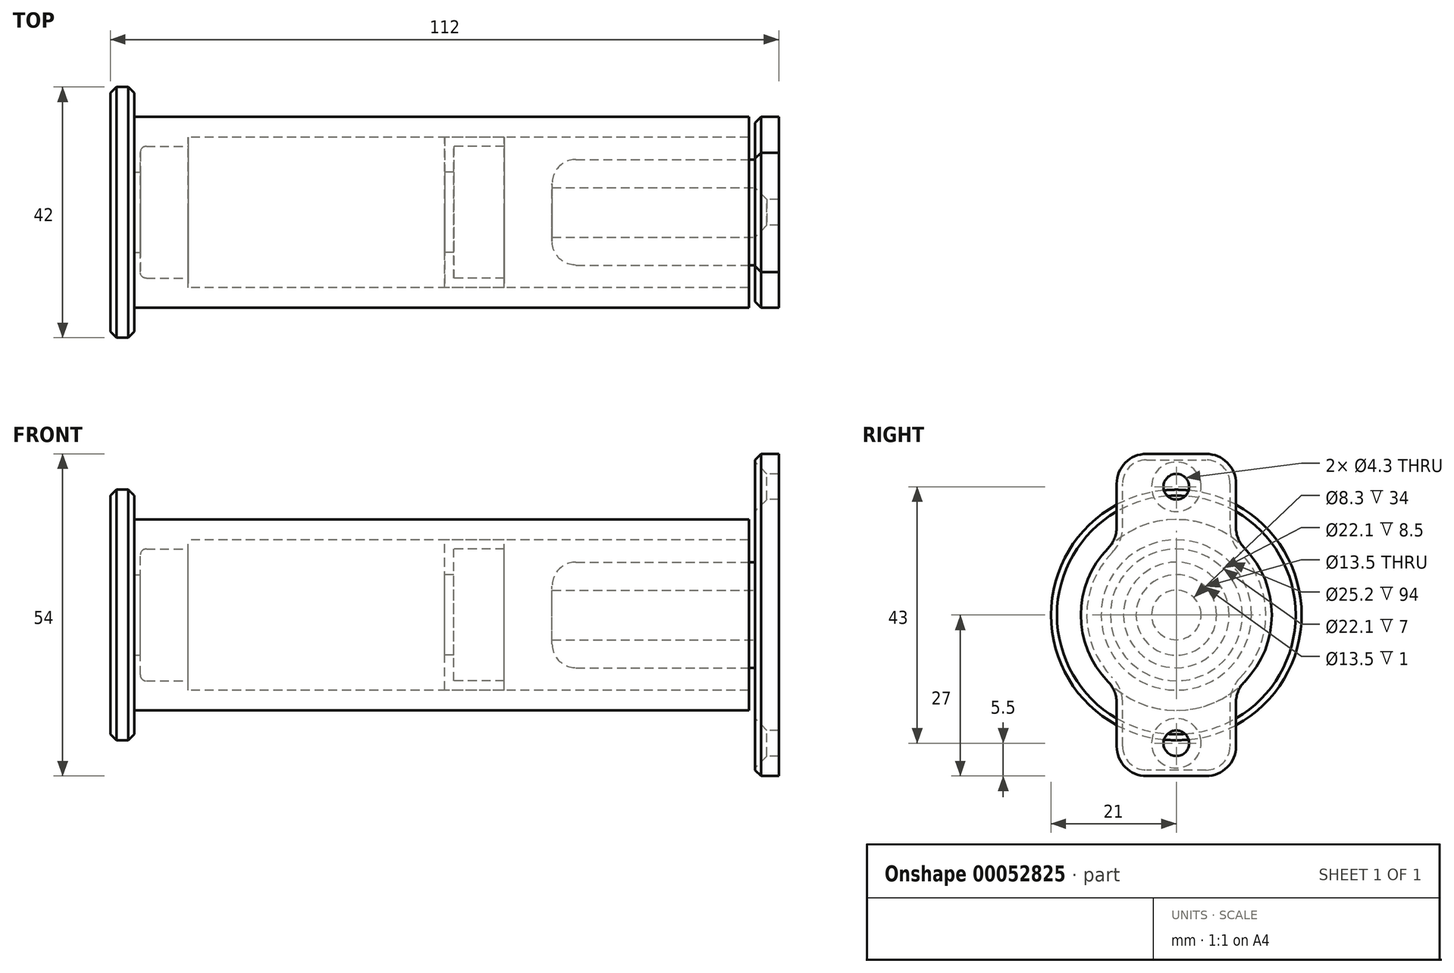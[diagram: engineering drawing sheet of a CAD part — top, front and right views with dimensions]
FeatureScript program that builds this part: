
annotation { "Feature Type Name" : "Feature", "Feature Type Description" : "" }
export const myFeature = defineFeature(function(context is Context, id is Id, definition is map)
    precondition{}
    {
        {
            var Q0;
            Q0=qCreatedBy(makeId("Right.planeOp"),FACE);
            var sketch = newSketch(context, id + "F0", { "sketchPlane" : qUnion([Q0])});
            skCircle(sketch, "E0", {"center": v(0, 0) * mm, "radius": 16 * mm});
            skCircle(sketch, "E1.0", {"center": v(0, 0) * mm, "radius": 12.6 * mm});
            skSolve(sketch);
        }
        {
            var Q0;
            Q0=makeQuery(id+"F0.imprint","IMPRINT",FACE,{"disambiguationData":[TD([[makeQuery(id+"F0.imprint","IMPRINT",EDGE,{"derivedFrom":sQuery(id+"F0.wireOp",EDGE,"E0")}),1.0]])]});
            extrude(context, id + "F1", {"entities" : qUnion([Q0]), "endBound" : BoundingType.SYMMETRIC, "depth" : 104 * mm});
        }
        {
            var Q0;
            Q0=makeQuery(id+"F1.opExtrude","CAP_FACE",FACE,{"disambiguationData":[OSD([sQuery(id+"F0.wireOp",EDGE,"E0"),sQuery(id+"F0.wireOp",EDGE,"E1.0")])],"isStart":true});
            var sketch = newSketch(context, id + "F2", { "sketchPlane" : qUnion([Q0])});
            skCircle(sketch, "E2.0", {"center": v(0, 0) * mm, "radius": 21 * mm});
            skSolve(sketch);
        }
        {
            var Q0;
            Q0=makeQuery(id+"F2.imprint","IMPRINT",FACE,{"disambiguationData":[TD([[makeQuery(id+"F2.imprint","IMPRINT",EDGE,{"derivedFrom":sQuery(id+"F2.wireOp",EDGE,"E2.0")}),1.0]])]});
            var Q1;
            Q1=makeQuery(id+"F2.imprint","IMPRINT",FACE,{"disambiguationData":[TD([[makeQuery(id+"F2.imprint","IMPRINT",EDGE,{"derivedFrom":makeQuery(id+"F1.opExtrude","CAP_EDGE",EDGE,{"disambiguationData":[OSD([sQuery(id+"F0.wireOp",EDGE,"E1.0")])],"isStart":true})}),-1.0]])]});
            var Q2;
            Q2=makeQuery(id+"F2.imprint","IMPRINT",FACE,{"disambiguationData":[TD([[makeQuery(id+"F2.imprint","IMPRINT",EDGE,{"derivedFrom":makeQuery(id+"F1.opExtrude","CAP_EDGE",EDGE,{"disambiguationData":[OSD([sQuery(id+"F0.wireOp",EDGE,"E0")])],"isStart":true})}),-1.0]])]});
            extrude(context, id + "F3", {"entities" : qUnion([Q0, Q1, Q2]), "depth" : 4 * mm});
        }
        {
            var Q0;
            Q0=makeQuery(id+"F2.imprint","IMPRINT",FACE,{"disambiguationData":[TD([[makeQuery(id+"F2.imprint","IMPRINT",EDGE,{"derivedFrom":makeQuery(id+"F1.opExtrude","CAP_EDGE",EDGE,{"disambiguationData":[OSD([sQuery(id+"F0.wireOp",EDGE,"E1.0")])],"isStart":true})}),-1.0]])]});
            extrude(context, id + "F4", {"entities" : qUnion([Q0]), "operationType" : NewBodyOperationType.ADD, "oppositeDirection" : true, "depth" : 9 * mm});
        }
        {
            var Q0;
            Q0=makeQuery(id+"F4.opExtrude","CAP_FACE",FACE,{"disambiguationData":[OSD([sQuery(id+"F0.wireOp",EDGE,"E1.0")])],"isStart":false});
            var sketch = newSketch(context, id + "F5", { "sketchPlane" : qUnion([Q0])});
            skCircle(sketch, "E3", {"center": v(0, 0) * mm, "radius": 11.05 * mm});
            skCircle(sketch, "E4", {"center": v(0, 0) * mm, "radius": 6.75 * mm});
            skSolve(sketch);
        }
        {
            var Q0;
            Q0=makeQuery(id+"F5.imprint","IMPRINT",FACE,{"disambiguationData":[TD([[makeQuery(id+"F5.imprint","IMPRINT",EDGE,{"derivedFrom":sQuery(id+"F5.wireOp",EDGE,"E3")}),1.0]])]});
            extrude(context, id + "F6", {"entities" : qUnion([Q0]), "operationType" : NewBodyOperationType.REMOVE, "oppositeDirection" : true, "depth" : 8 * mm});
        }
        {
            var Q0;
            Q0=makeQuery(id+"F6.boolean.opBoolean","SPLIT",FACE,{"disambiguationData":[TD([makeQuery(id+"F6.opExtrude","SWEPT_FACE",FACE,{"disambiguationData":[OSD([sQuery(id+"F5.wireOp",EDGE,"E4")])]})])],"derivedFrom":makeQuery(id+"F4.opExtrude","CAP_FACE",FACE,{"disambiguationData":[OSD([sQuery(id+"F0.wireOp",EDGE,"E1.0")])],"isStart":false})});
            extrude(context, id + "F7", {"entities" : qUnion([Q0]), "operationType" : NewBodyOperationType.REMOVE, "oppositeDirection" : true, "depth" : 9 * mm});
        }
        {
            var Q0;
            Q0=qCreatedBy(makeId("Right.planeOp"),FACE);
            var sketch = newSketch(context, id + "F8", { "sketchPlane" : qUnion([Q0])});
            skCircle(sketch, "E5.0", {"center": v(0, 0) * mm, "radius": 12.6 * mm});
            skCircle(sketch, "E5.1", {"center": v(0, 0) * mm, "radius": 11.05 * mm});
            skCircle(sketch, "E5.2", {"center": v(0, 0) * mm, "radius": 6.75 * mm});
            skSolve(sketch);
        }
        {
            var Q0;
            Q0=makeQuery(id+"F8.imprint","IMPRINT",FACE,{"disambiguationData":[TD([[makeQuery(id+"F8.imprint","IMPRINT",EDGE,{"derivedFrom":sQuery(id+"F8.wireOp",EDGE,"E5.0")}),1.0]])]});
            extrude(context, id + "F9", {"entities" : qUnion([Q0]), "depth" : 10 * mm});
        }
        {
            var Q0;
            Q0=makeQuery(id+"F8.imprint","IMPRINT",FACE,{"disambiguationData":[TD([[makeQuery(id+"F8.imprint","IMPRINT",EDGE,{"derivedFrom":sQuery(id+"F8.wireOp",EDGE,"E5.1")}),1.0]])]});
            extrude(context, id + "F10", {"entities" : qUnion([Q0]), "operationType" : NewBodyOperationType.ADD, "depth" : 1.5 * mm});
        }
        {
            var Q0;
            Q0=makeQuery(id+"F1.opExtrude","CAP_FACE",FACE,{"disambiguationData":[OSD([sQuery(id+"F0.wireOp",EDGE,"E0"),sQuery(id+"F0.wireOp",EDGE,"E1.0")])],"isStart":false});
            var sketch = newSketch(context, id + "F11", { "sketchPlane" : qUnion([Q0])});
            skCircle(sketch, "E6.0", {"center": v(0, 0) * mm, "radius": 16 * mm});
            skLineSegment(sketch, "E7.rect.bottom", {"start": v(5, -27) * mm, "end": v(-5, -27) * mm});
            skLineSegment(sketch, "E7.rect.top", {"start": v(5, 27) * mm, "end": v(-5, 27) * mm});
            skLineSegment(sketch, "E8", {"start": v(-16, 0) * mm, "end": v(16, 0) * mm, "construction": true});
            skLineSegment(sketch, "E9", {"start": v(0, -16) * mm, "end": v(0, -27) * mm, "construction": true});
            skCircle(sketch, "E10", {"center": v(0, -21.5) * mm, "radius": 2.15 * mm});
            skCircle(sketch, "E11.MirrorC", {"center": v(0, 21.5) * mm, "radius": 2.15 * mm});
            skLineSegment(sketch, "E12", {"start": v(10, -12.49) * mm, "end": v(10, -22) * mm});
            skLineSegment(sketch, "E13", {"start": v(-10, -22) * mm, "end": v(-10, -12.49) * mm});
            skLineSegment(sketch, "E14.MirrorCS", {"start": v(10, 12.49) * mm, "end": v(10, 22) * mm});
            skLineSegment(sketch, "E15.MirrorCS", {"start": v(-10, 22) * mm, "end": v(-10, 12.49) * mm});
            skPoint(sketch, "E16.visualSharp", {"position": v(10, 27) * mm});
            skArc(sketch, "E16.filletArc", {"start": v(10, 22) * mm, "mid": v(8.54, 25.54) * mm, "end": v(5, 27) * mm});
            skPoint(sketch, "E17.visualSharp", {"position": v(-10, 27) * mm});
            skArc(sketch, "E17.filletArc", {"start": v(-5, 27) * mm, "mid": v(-8.54, 25.54) * mm, "end": v(-10, 22) * mm});
            skPoint(sketch, "E18.visualSharp", {"position": v(-10, -27) * mm});
            skArc(sketch, "E18.filletArc", {"start": v(-10, -22) * mm, "mid": v(-8.54, -25.54) * mm, "end": v(-5, -27) * mm});
            skPoint(sketch, "E19.visualSharp", {"position": v(10, -27) * mm});
            skArc(sketch, "E19.filletArc", {"start": v(5, -27) * mm, "mid": v(8.54, -25.54) * mm, "end": v(10, -22) * mm});
            skCircle(sketch, "E20", {"center": v(0, 0) * mm, "radius": 4.15 * mm});
            skCircle(sketch, "E21.0", {"center": v(0, 0) * mm, "radius": 8.85 * mm});
            skSolve(sketch);
        }
        {
            var Q0;
            Q0=makeQuery(id+"F11.imprint","IMPRINT",FACE,{"disambiguationData":[TD([[makeQuery(id+"F11.imprint","IMPRINT",EDGE,{"derivedFrom":sQuery(id+"F11.wireOp",EDGE,"E7.rect.bottom")}),-1.0]])]});
            var Q1;
            Q1=makeQuery(id+"F11.imprint","IMPRINT",FACE,{"disambiguationData":[TD([[makeQuery(id+"F11.imprint","IMPRINT",EDGE,{"derivedFrom":sQuery(id+"F11.wireOp",EDGE,"E7.rect.top")}),1.0]])]});
            var Q2;
            Q2=makeQuery(id+"F11.imprint","IMPRINT",FACE,{"disambiguationData":[TD([[makeQuery(id+"F11.imprint","IMPRINT",EDGE,{"derivedFrom":sQuery(id+"F11.wireOp",EDGE,"E20")}),1.0]])]});
            var Q3;
            Q3=makeQuery(id+"F11.imprint","IMPRINT",FACE,{"disambiguationData":[TD([[makeQuery(id+"F11.imprint","IMPRINT",EDGE,{"derivedFrom":sQuery(id+"F11.wireOp",EDGE,"E21.0")}),-1.0]])]});
            var Q4;
            Q4=makeQuery(id+"F11.imprint","IMPRINT",FACE,{"disambiguationData":[TD([[makeQuery(id+"F11.imprint","IMPRINT",EDGE,{"derivedFrom":sQuery(id+"F11.wireOp",EDGE,"E20")}),-1.0]])]});
            var Q5;
            Q5=makeQuery(id+"F11.imprint","IMPRINT",FACE,{"disambiguationData":[TD([[makeQuery(id+"F11.imprint","IMPRINT",EDGE,{"derivedFrom":makeQuery(id+"F1.opExtrude","CAP_EDGE",EDGE,{"disambiguationData":[OSD([sQuery(id+"F0.wireOp",EDGE,"E1.0")])],"isStart":false})}),-1.0]])]});
            extrude(context, id + "F12", {"entities" : qUnion([Q0, Q1, Q2, Q3, Q4, Q5]), "depth" : 4 * mm});
        }
        {
            var Q0;
            Q0=makeQuery(id+"F11.imprint","IMPRINT",FACE,{"disambiguationData":[TD([[makeQuery(id+"F11.imprint","IMPRINT",EDGE,{"derivedFrom":sQuery(id+"F11.wireOp",EDGE,"E20")}),-1.0]])]});
            extrude(context, id + "F13", {"entities" : qUnion([Q0]), "operationType" : NewBodyOperationType.ADD, "oppositeDirection" : true, "depth" : 34 * mm});
        }
        {
            var Q0;
            Q0=makeQuery(id+"F13.opExtrude","CAP_EDGE",EDGE,{"disambiguationData":[OSD([sQuery(id+"F11.wireOp",EDGE,"E21.0")])],"isStart":false});
            var Q1;
            Q1=makeQuery(id+"F13.opExtrude","CAP_EDGE",EDGE,{"disambiguationData":[OSD([sQuery(id+"F11.wireOp",EDGE,"E21.0")])],"isStart":true});
            fillet(context, id + "F14", {"entities" : qUnion([Q0, Q1]), "radius" : 4 * mm, "tangentPropagation" : true, "allowEdgeOverflow" : false});
        }
        {
            var Q0;
            Q0=makeQuery(id+"F12.opExtrude","SWEPT_EDGE",EDGE,{"disambiguationData":[OSD([sQuery(id+"F11.wireOp",EDGE,"E6.0"),sQuery(id+"F11.wireOp",EDGE,"E15.MirrorCS")])]});
            var Q1;
            Q1=makeQuery(id+"F12.opExtrude","SWEPT_EDGE",EDGE,{"disambiguationData":[OSD([sQuery(id+"F11.wireOp",EDGE,"E6.0"),sQuery(id+"F11.wireOp",EDGE,"E13")])]});
            var Q2;
            Q2=makeQuery(id+"F12.opExtrude","SWEPT_EDGE",EDGE,{"disambiguationData":[OSD([sQuery(id+"F11.wireOp",EDGE,"E6.0"),sQuery(id+"F11.wireOp",EDGE,"E12")])]});
            var Q3;
            Q3=makeQuery(id+"F12.opExtrude","SWEPT_EDGE",EDGE,{"disambiguationData":[OSD([sQuery(id+"F11.wireOp",EDGE,"E6.0"),sQuery(id+"F11.wireOp",EDGE,"E14.MirrorCS")])]});
            fillet(context, id + "F15", {"entities" : qUnion([Q0, Q1, Q2, Q3]), "radius" : 5 * mm, "tangentPropagation" : true, "allowEdgeOverflow" : false});
        }
        {
            var Q0;
            Q0=makeQuery(id+"F12.opExtrude","CAP_EDGE",EDGE,{"disambiguationData":[OSD([sQuery(id+"F11.wireOp",EDGE,"E12")])],"isStart":true});
            chamfer(context, id + "F16", {"entities" : qUnion([Q0]), "width" : 1 * mm, "tangentPropagation" : true});
        }
        {
            var Q0;
            Q0=makeQuery(id+"F3.opExtrude","CAP_EDGE",EDGE,{"disambiguationData":[OSD([sQuery(id+"F2.wireOp",EDGE,"E2.0")])],"isStart":false});
            var Q1;
            Q1=makeQuery(id+"F3.opExtrude","CAP_EDGE",EDGE,{"disambiguationData":[OSD([sQuery(id+"F2.wireOp",EDGE,"E2.0")])],"isStart":true});
            chamfer(context, id + "F17", {"entities" : qUnion([Q0, Q1]), "width" : 1 * mm, "tangentPropagation" : true});
        }
        {
            var Q0;
            Q0=makeQuery(id+"F12.opExtrude","CAP_EDGE",EDGE,{"disambiguationData":[OSD([sQuery(id+"F11.wireOp",EDGE,"E11.MirrorC")])],"isStart":true});
            var Q1;
            Q1=makeQuery(id+"F12.opExtrude","CAP_EDGE",EDGE,{"disambiguationData":[OSD([sQuery(id+"F11.wireOp",EDGE,"E10")])],"isStart":true});
            chamfer(context, id + "F18", {"entities" : qUnion([Q0, Q1]), "width" : 2 * mm, "tangentPropagation" : true});
        }
        {
            var Q0;
            Q0=makeQuery(id+"F4.opExtrude","CAP_EDGE",EDGE,{"disambiguationData":[OSD([sQuery(id+"F0.wireOp",EDGE,"E1.0")])],"isStart":true});
            var Q1;
            Q1=makeQuery(id+"F10.opExtrude","CAP_EDGE",EDGE,{"disambiguationData":[OSD([sQuery(id+"F8.wireOp",EDGE,"E5.1")])],"isStart":false});
            var Q2;
            Q2=makeQuery(id+"F6.boolean.opBoolean","COPY",EDGE,{"derivedFrom":makeQuery(id+"F6.opExtrude","CAP_EDGE",EDGE,{"disambiguationData":[OSD([sQuery(id+"F5.wireOp",EDGE,"E3")])],"isStart":false})});
            fillet(context, id + "F19", {"entities" : qUnion([Q0, Q1, Q2]), "radius" : 1 * mm, "tangentPropagation" : true, "allowEdgeOverflow" : false});
        }
        {
            var Q0;
            Q0=makeQuery(id+"F1.opExtrude","CAP_FACE",FACE,{"disambiguationData":[OSD([sQuery(id+"F0.wireOp",EDGE,"E0"),sQuery(id+"F0.wireOp",EDGE,"E1.0")])],"isStart":false});
            extrude(context, id + "F20", {"entities" : qUnion([Q0]), "operationType" : NewBodyOperationType.REMOVE, "oppositeDirection" : true, "depth" : 1 * mm});
        }
    });
